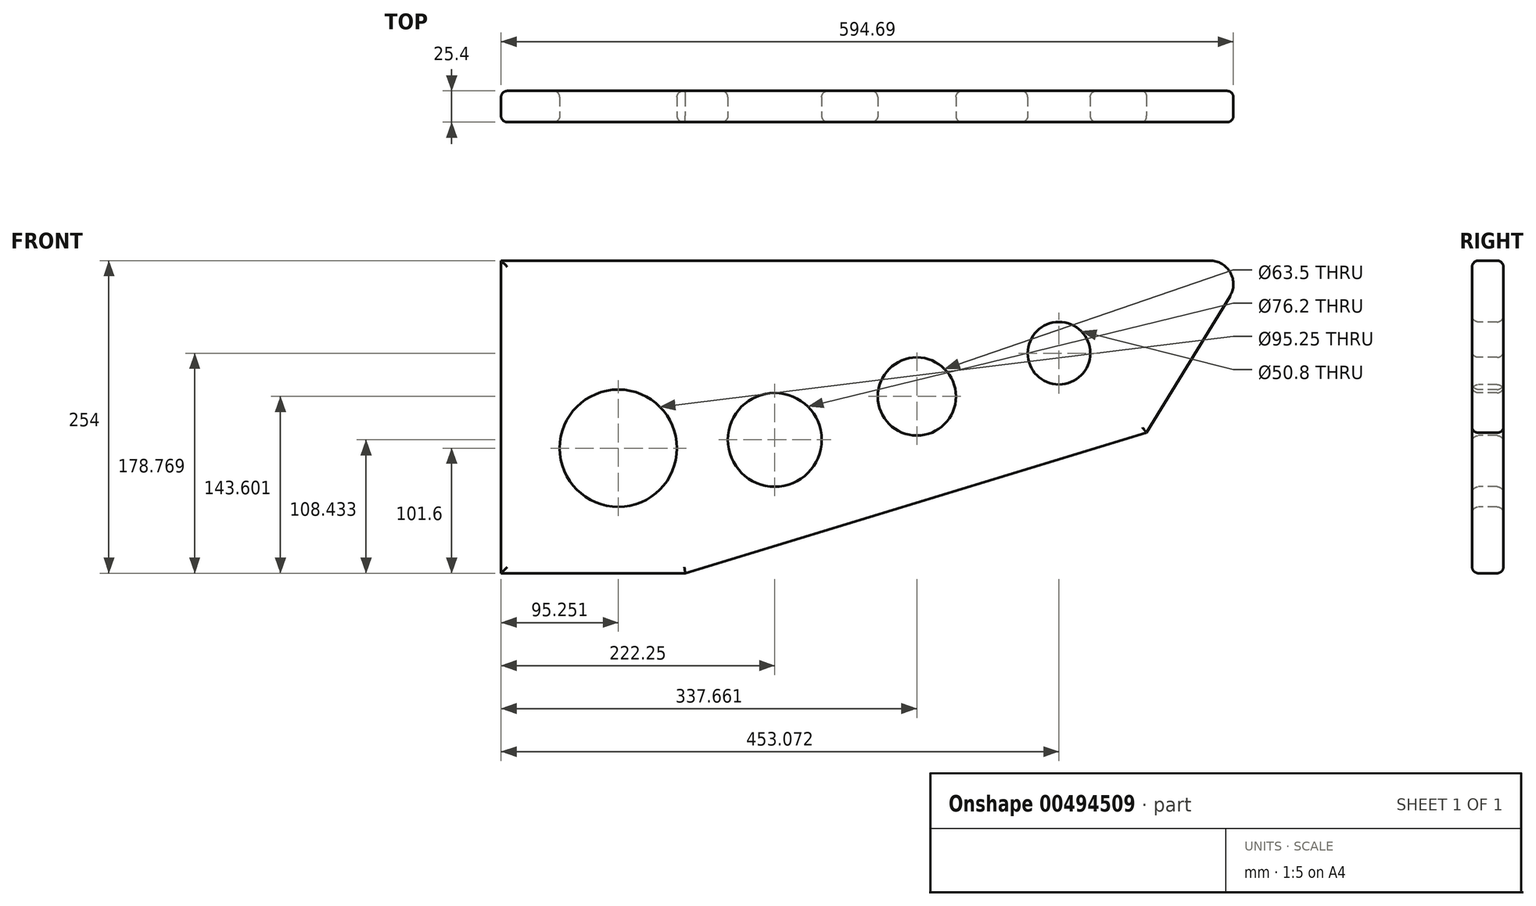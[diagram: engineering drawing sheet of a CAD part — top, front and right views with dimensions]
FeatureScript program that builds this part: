
annotation { "Feature Type Name" : "Feature", "Feature Type Description" : "" }
export const myFeature = defineFeature(function(context is Context, id is Id, definition is map)
    precondition{}
    {
        {
            var Q0;
            Q0=qCreatedBy(makeId("Front.planeOp"),FACE);
            var sketch = newSketch(context, id + "F0", { "sketchPlane" : qUnion([Q0])});
            skLineSegment(sketch, "E0", {"start": v(-79.75, 0) * mm, "end": v(-79.75, 254) * mm});
            skLineSegment(sketch, "E1", {"start": v(-79.75, 254) * mm, "end": v(529.85, 254) * mm});
            skLineSegment(sketch, "E2", {"start": v(-79.75, 0) * mm, "end": v(69.86, 0) * mm});
            skLineSegment(sketch, "E3", {"start": v(69.86, 0) * mm, "end": v(444.43, 114.14) * mm});
            skLineSegment(sketch, "E4", {"start": v(444.43, 114.14) * mm, "end": v(529.85, 254) * mm});
            skCircle(sketch, "E5", {"center": v(15.5, 101.6) * mm, "radius": 47.63 * mm});
            skCircle(sketch, "E6", {"center": v(142.5, 108.43) * mm, "radius": 38.1 * mm});
            skCircle(sketch, "E7", {"center": v(257.91, 143.6) * mm, "radius": 31.75 * mm});
            skCircle(sketch, "E8", {"center": v(373.32, 178.77) * mm, "radius": 25.4 * mm});
            skSolve(sketch);
        }
        {
            var Q0;
            Q0 = qSketchRegion(id + "F0", true);
            extrude(context, id + "F1", {"entities" : qUnion([Q0]), "oppositeDirection" : true, "depth" : 25.4 * mm});
        }
        {
            var Q0;
            Q0=makeQuery(id+"F1.opExtrude","SWEPT_EDGE",EDGE,{"disambiguationData":[OSD([sQuery(id+"F0.wireOp",EDGE,"E1"),sQuery(id+"F0.wireOp",EDGE,"E4")])]});
            fillet(context, id + "F2", {"entities" : qUnion([Q0]), "radius" : 19.05 * mm, "tangentPropagation" : true, "allowEdgeOverflow" : false});
        }
        {
            var Q0;
            Q0=makeQuery(id+"F1.opExtrude","CAP_EDGE",EDGE,{"disambiguationData":[OSD([sQuery(id+"F0.wireOp",EDGE,"E8")])],"isStart":true});
            var Q1;
            Q1=makeQuery(id+"F1.opExtrude","CAP_EDGE",EDGE,{"disambiguationData":[OSD([sQuery(id+"F0.wireOp",EDGE,"E7")])],"isStart":true});
            var Q2;
            Q2=makeQuery(id+"F1.opExtrude","CAP_EDGE",EDGE,{"disambiguationData":[OSD([sQuery(id+"F0.wireOp",EDGE,"E6")])],"isStart":true});
            var Q3;
            Q3=makeQuery(id+"F1.opExtrude","CAP_EDGE",EDGE,{"disambiguationData":[OSD([sQuery(id+"F0.wireOp",EDGE,"E5")])],"isStart":true});
            var Q4;
            Q4=makeQuery(id+"F1.opExtrude","CAP_FACE",FACE,{"disambiguationData":[OSD([sQuery(id+"F0.wireOp",EDGE,"E0"),sQuery(id+"F0.wireOp",EDGE,"E1"),sQuery(id+"F0.wireOp",EDGE,"E2"),sQuery(id+"F0.wireOp",EDGE,"E3"),sQuery(id+"F0.wireOp",EDGE,"E4"),sQuery(id+"F0.wireOp",EDGE,"E5"),sQuery(id+"F0.wireOp",EDGE,"E6"),sQuery(id+"F0.wireOp",EDGE,"E7"),sQuery(id+"F0.wireOp",EDGE,"E8")])],"isStart":true});
            fillet(context, id + "F3", {"entities" : qUnion([Q0, Q1, Q2, Q3, Q4]), "radius" : 5.08 * mm, "tangentPropagation" : true, "allowEdgeOverflow" : false});
        }
        {
            var Q0;
            Q0=makeQuery(id+"F1.opExtrude","CAP_FACE",FACE,{"disambiguationData":[OSD([sQuery(id+"F0.wireOp",EDGE,"E0"),sQuery(id+"F0.wireOp",EDGE,"E1"),sQuery(id+"F0.wireOp",EDGE,"E2"),sQuery(id+"F0.wireOp",EDGE,"E3"),sQuery(id+"F0.wireOp",EDGE,"E4"),sQuery(id+"F0.wireOp",EDGE,"E5"),sQuery(id+"F0.wireOp",EDGE,"E6"),sQuery(id+"F0.wireOp",EDGE,"E7"),sQuery(id+"F0.wireOp",EDGE,"E8")])],"isStart":false});
            fillet(context, id + "F4", {"entities" : qUnion([Q0]), "radius" : 5.08 * mm, "tangentPropagation" : true, "allowEdgeOverflow" : false});
        }
    });
